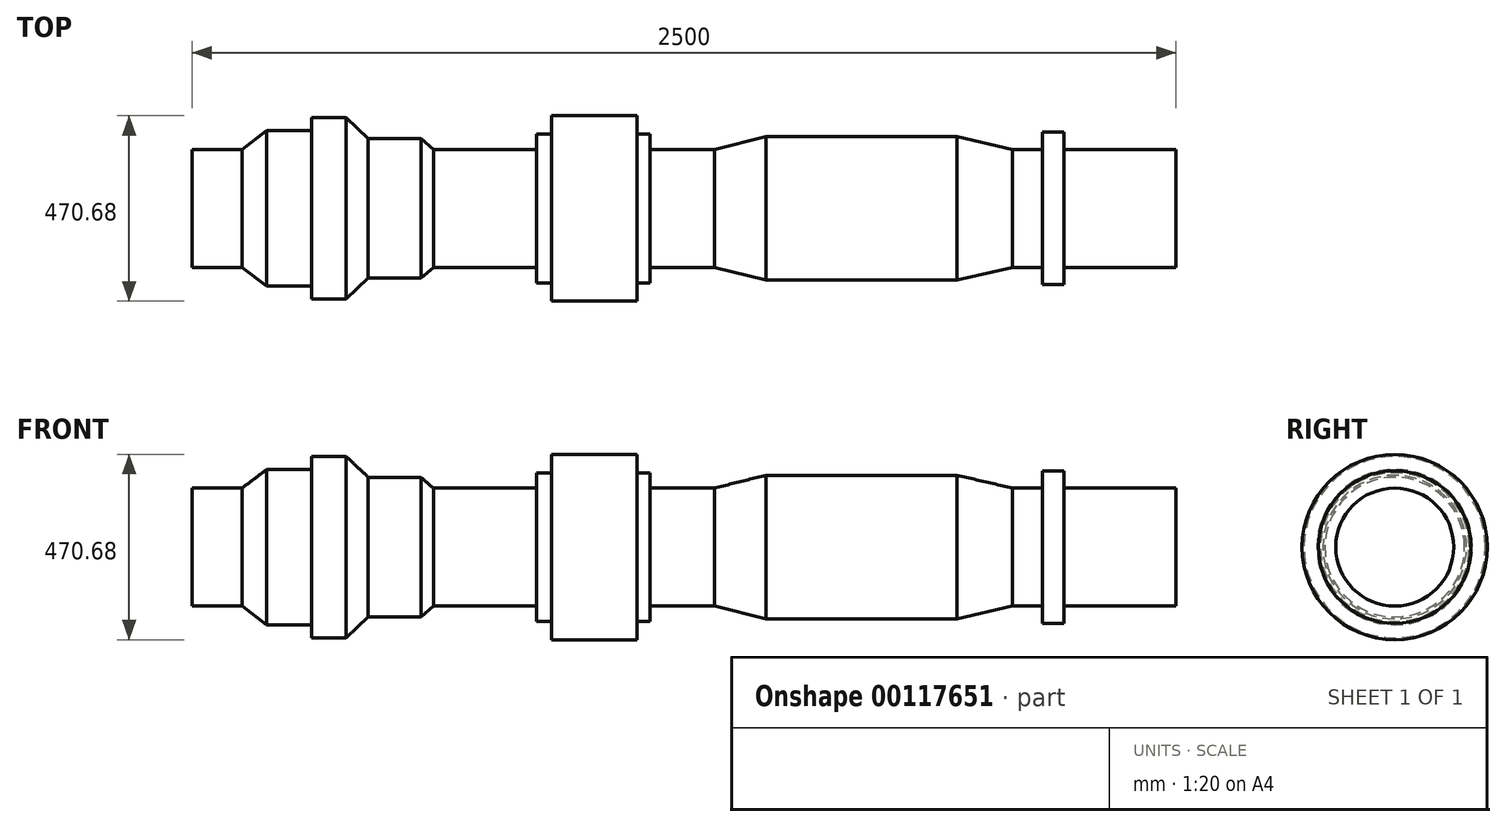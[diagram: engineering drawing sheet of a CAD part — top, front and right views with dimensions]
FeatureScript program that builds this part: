
annotation { "Feature Type Name" : "Feature", "Feature Type Description" : "" }
export const myFeature = defineFeature(function(context is Context, id is Id, definition is map)
    precondition{}
    {
        {
            var Q0;
            Q0=qCreatedBy(makeId("Top.planeOp"),FACE);
            var sketch = newSketch(context, id + "F0", { "sketchPlane" : qUnion([Q0])});
            skLineSegment(sketch, "E0.bottom", {"start": v(-1250, 0) * mm, "end": v(1250, 0) * mm});
            skLineSegment(sketch, "E0.top", {"start": v(-1250, 150) * mm, "end": v(1250, 150) * mm});
            skLineSegment(sketch, "E0.left", {"start": v(-1250, 0) * mm, "end": v(-1250, 150) * mm});
            skLineSegment(sketch, "E0.right", {"start": v(1250, 0) * mm, "end": v(1250, 150) * mm});
            skLineSegment(sketch, "E1.bottom", {"start": v(0, 0) * mm, "end": v(0, 0) * mm});
            skLineSegment(sketch, "E1.top", {"start": v(0, 0) * mm, "end": v(0, 0) * mm});
            skLineSegment(sketch, "E1.left", {"start": v(0, 0) * mm, "end": v(0, 0) * mm});
            skLineSegment(sketch, "E1.right", {"start": v(0, 0) * mm, "end": v(0, 0) * mm});
            skLineSegment(sketch, "E2", {"start": v(-1123.07, 150) * mm, "end": v(-1060.26, 197.33) * mm});
            skLineSegment(sketch, "E3", {"start": v(-1060.26, 197.33) * mm, "end": v(-946.21, 197.33) * mm});
            skLineSegment(sketch, "E4", {"start": v(-946.21, 197.33) * mm, "end": v(-946.21, 230.38) * mm});
            skLineSegment(sketch, "E5", {"start": v(-946.21, 230.38) * mm, "end": v(-858.61, 230.38) * mm});
            skLineSegment(sketch, "E6", {"start": v(-858.61, 230.38) * mm, "end": v(-802.42, 177.5) * mm});
            skLineSegment(sketch, "E7", {"start": v(-802.42, 177.5) * mm, "end": v(-668.54, 177.5) * mm});
            skLineSegment(sketch, "E8", {"start": v(-668.54, 177.5) * mm, "end": v(-637.14, 150) * mm});
            skLineSegment(sketch, "E9", {"start": v(-637.14, 150) * mm, "end": v(-374.34, 150) * mm});
            skLineSegment(sketch, "E10", {"start": v(-374.34, 150) * mm, "end": v(-374.34, 189.06) * mm});
            skLineSegment(sketch, "E11", {"start": v(-374.34, 189.06) * mm, "end": v(-336.32, 189.06) * mm});
            skLineSegment(sketch, "E12", {"start": v(-336.32, 189.06) * mm, "end": v(-336.32, 235.34) * mm});
            skLineSegment(sketch, "E13", {"start": v(-336.32, 235.34) * mm, "end": v(-119.8, 235.34) * mm});
            skLineSegment(sketch, "E14", {"start": v(-119.8, 235.34) * mm, "end": v(-119.8, 189.06) * mm});
            skLineSegment(sketch, "E15", {"start": v(-119.8, 189.06) * mm, "end": v(-86.75, 189.06) * mm});
            skLineSegment(sketch, "E16", {"start": v(-86.75, 189.06) * mm, "end": v(-86.75, 150) * mm});
            skLineSegment(sketch, "E17", {"start": v(-86.75, 150) * mm, "end": v(76.88, 150) * mm});
            skLineSegment(sketch, "E18", {"start": v(76.88, 150) * mm, "end": v(207.46, 182.45) * mm});
            skLineSegment(sketch, "E19", {"start": v(207.46, 182.45) * mm, "end": v(693.38, 182.45) * mm});
            skLineSegment(sketch, "E20", {"start": v(693.38, 182.45) * mm, "end": v(833.87, 150) * mm});
            skLineSegment(sketch, "E21", {"start": v(833.87, 150) * mm, "end": v(909.9, 150) * mm});
            skLineSegment(sketch, "E22", {"start": v(909.9, 150) * mm, "end": v(909.9, 194.02) * mm});
            skLineSegment(sketch, "E23", {"start": v(909.9, 194.02) * mm, "end": v(964.45, 194.02) * mm});
            skLineSegment(sketch, "E24", {"start": v(964.45, 194.02) * mm, "end": v(964.45, 150) * mm});
            skSolve(sketch);
        }
        {
            var Q0;
            Q0 = qSketchRegion(id + "F0", true);
            var Q1;
            Q1=sQuery(id+"F0.wireOp",EDGE,"E0.bottom");
            revolve(context, id + "F1", {"entities" : qUnion([Q0]), "axis" : qUnion([Q1]), "revolveType" : RevolveType.FULL});
        }
    });
